# Revit family: OTG-2
name_source: partatom
category: Plumbing Fixtures
revit_build: Autodesk Revit MEP 2016 (Build: 20150220_1215(x64)
units: mm (PartAtom-declared; Revit-internal decimal feet)

## family parameters
Cut with Voids When Loaded = No
Host = Face
OmniClass Number = 23.65.00.00
OmniClass Title = Supply and Distribution of Liquids and Gases
Part Type = Normal
Room Calculation Point = No
Round Connector Dimension = Use Diameter
Shared = Yes

## types (1)
- OTG-2
    Assembly Code = D2020
    CW Connection = Yes
    CWFU = 0
    Default Elevation = 0"
    Description = Outlet Temperature Gauge with 1 Inch NPT Outlet Tee Connections
    HW Connection = Yes
    HWFU = 0
    Manufacturer = Acorn Controls
    Material = Default
    Model = OTG-2
    OTG-2 -  Outlet Temperature Gauge with 1 Inch NPT Outlet Tee Connections = Yes
    Revised Date = 09/17/19
    Tempered Water Connection = Yes
    URL = http://www.acorneng.com
    Vent Connection = No
    WFU = 0
    Waste Connection = No

## geometry (parser evidence)
native form markers: Sweep x4
no freeform markers — native parametric forms only
